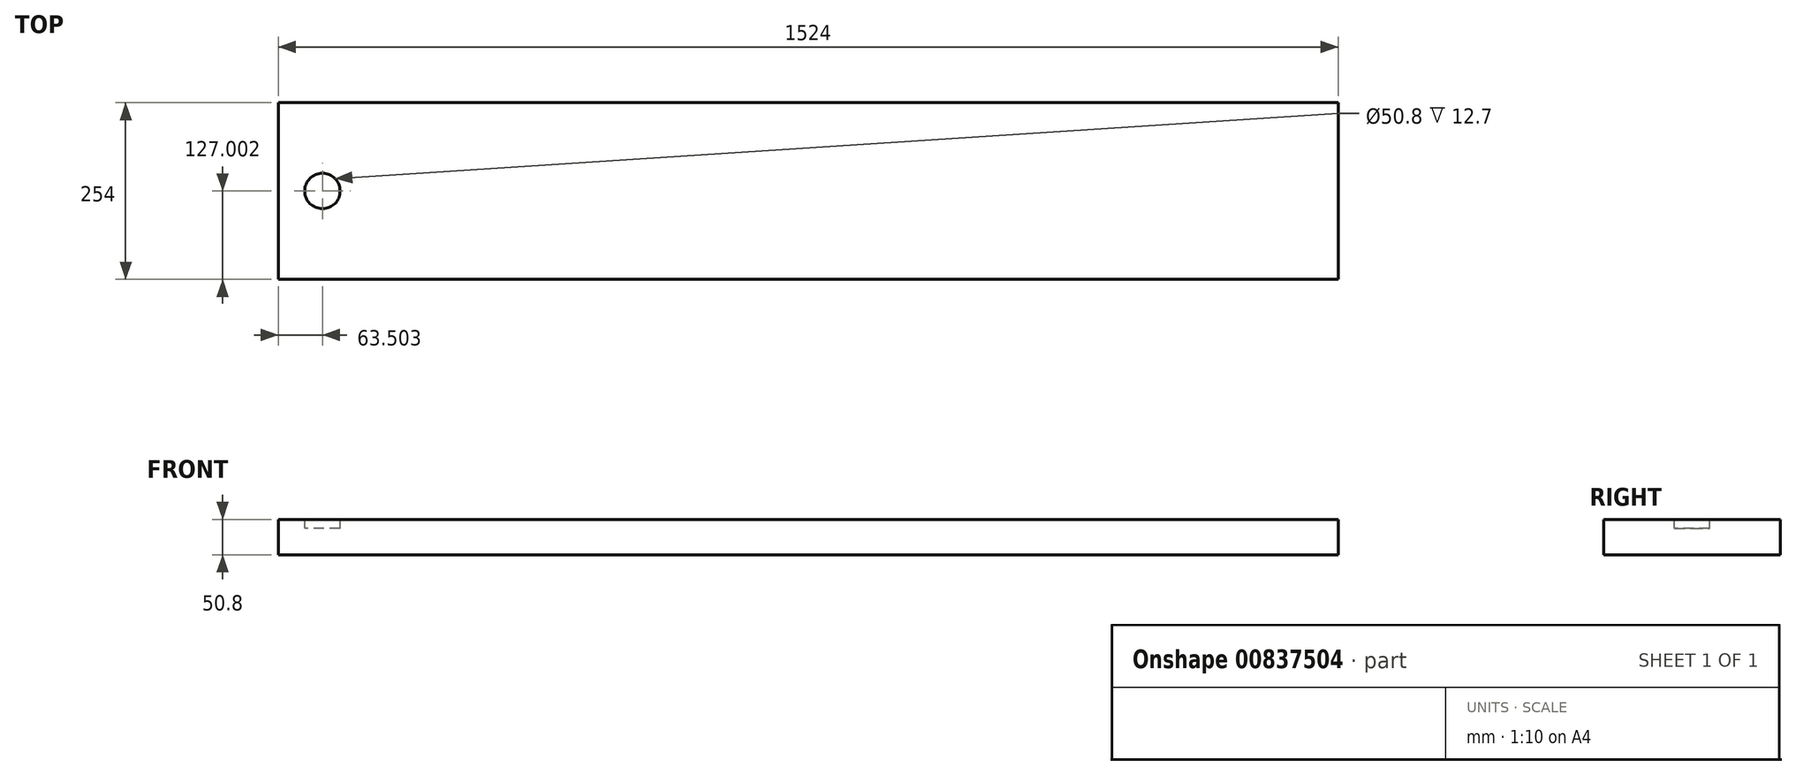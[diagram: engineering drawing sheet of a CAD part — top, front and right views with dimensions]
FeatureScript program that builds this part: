
annotation { "Feature Type Name" : "Feature", "Feature Type Description" : "" }
export const myFeature = defineFeature(function(context is Context, id is Id, definition is map)
    precondition{}
    {
        {
            var Q0;
            Q0=qCreatedBy(makeId("Top.planeOp"),FACE);
            var sketch = newSketch(context, id + "F0", { "sketchPlane" : qUnion([Q0])});
            skLineSegment(sketch, "E0.bottom", {"start": v(-130.2, 225.7) * mm, "end": v(1393.8, 225.7) * mm});
            skLineSegment(sketch, "E0.top", {"start": v(-130.2, -28.3) * mm, "end": v(1393.8, -28.3) * mm});
            skLineSegment(sketch, "E0.left", {"start": v(-130.2, 225.7) * mm, "end": v(-130.2, -28.3) * mm});
            skLineSegment(sketch, "E0.right", {"start": v(1393.8, 225.7) * mm, "end": v(1393.8, -28.3) * mm});
            skSolve(sketch);
        }
        {
            var Q0;
            Q0=makeQuery(id+"F0.imprint","IMPRINT",FACE,{"disambiguationData":[TD([[makeQuery(id+"F0.imprint","IMPRINT",EDGE,{"derivedFrom":sQuery(id+"F0.wireOp",EDGE,"E0.bottom")}),-1.0]])]});
            extrude(context, id + "F1", {"entities" : qUnion([Q0]), "endBound" : BoundingType.SYMMETRIC, "depth" : 50.8 * mm, "offsetDistance" : 25.4 * mm});
        }
        {
            var Q0;
            Q0=makeQuery(id+"F1.opExtrude","CAP_FACE",FACE,{"disambiguationData":[OSD([sQuery(id+"F0.wireOp",EDGE,"E0.bottom"),sQuery(id+"F0.wireOp",EDGE,"E0.top"),sQuery(id+"F0.wireOp",EDGE,"E0.left"),sQuery(id+"F0.wireOp",EDGE,"E0.right")])],"isStart":false});
            var sketch = newSketch(context, id + "F2", { "sketchPlane" : qUnion([Q0])});
            skCircle(sketch, "E1", {"center": v(-66.7, 98.7) * mm, "radius": 25.4 * mm});
            skSolve(sketch);
        }
        {
            var Q0;
            Q0=makeQuery(id+"F2.imprint","IMPRINT",FACE,{"disambiguationData":[TD([[makeQuery(id+"F2.imprint","IMPRINT",EDGE,{"derivedFrom":sQuery(id+"F2.wireOp",EDGE,"E1")}),1.0]])]});
            extrude(context, id + "F3", {"entities" : qUnion([Q0]), "operationType" : NewBodyOperationType.REMOVE, "oppositeDirection" : true, "depth" : 12.7 * mm, "offsetDistance" : 25.4 * mm});
        }
    });
